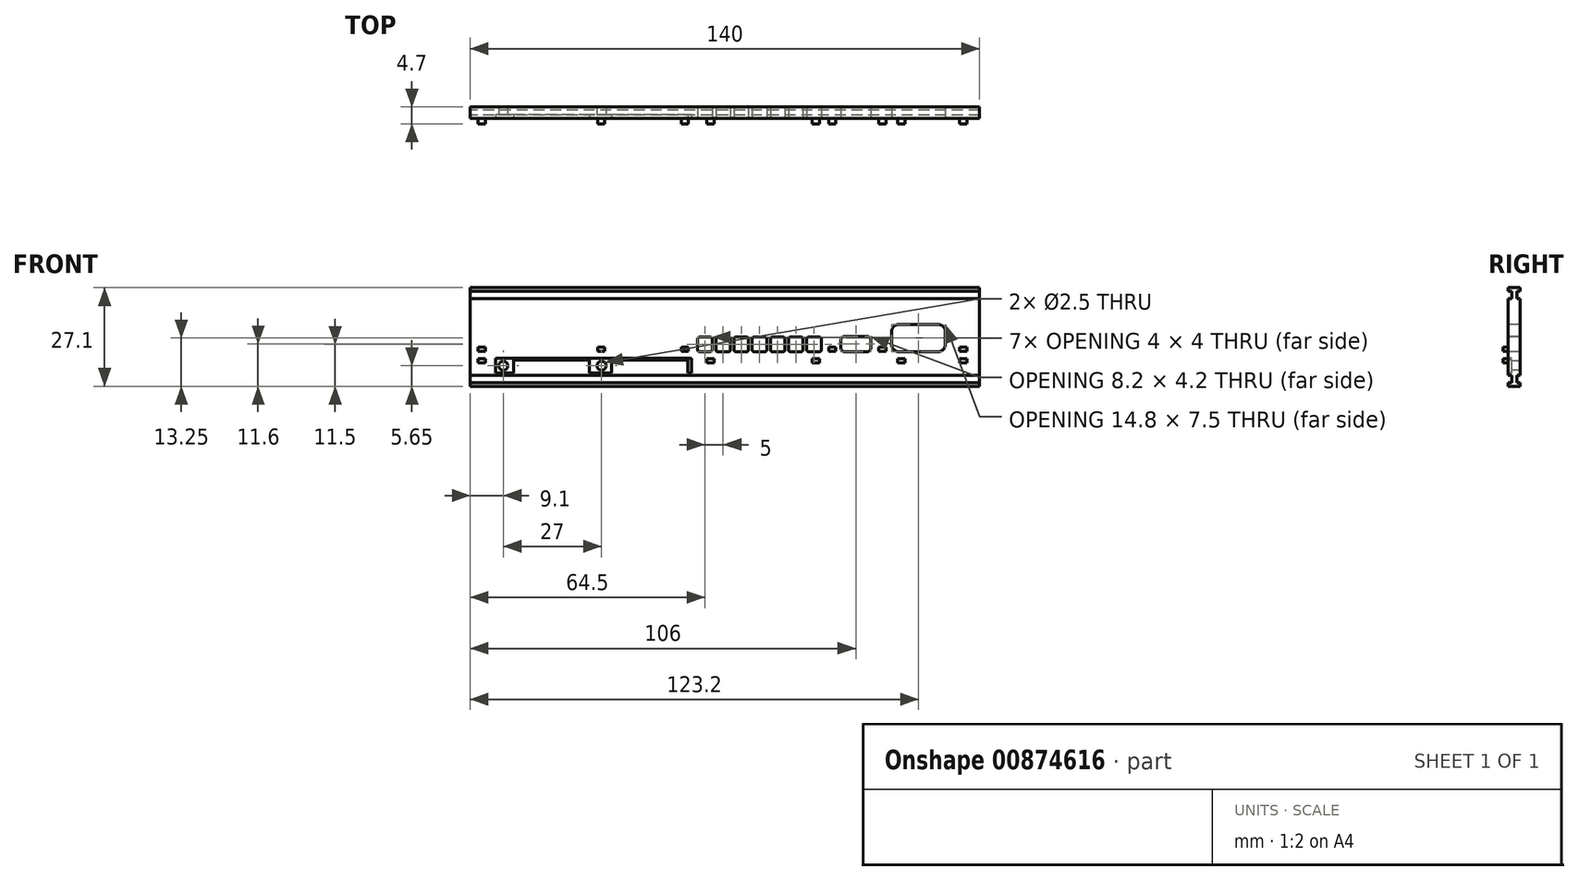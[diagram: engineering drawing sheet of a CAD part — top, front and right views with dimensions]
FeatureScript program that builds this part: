
annotation { "Feature Type Name" : "Feature", "Feature Type Description" : "" }
export const myFeature = defineFeature(function(context is Context, id is Id, definition is map)
    precondition{}
    {
        {
            var Q0;
            Q0=qCreatedBy(makeId("Right.planeOp"),FACE);
            var sketch = newSketch(context, id + "F0", { "sketchPlane" : qUnion([Q0])});
            skLineSegment(sketch, "E0", {"start": v(-1.6, 0) * mm, "end": v(-1.6, 10.55) * mm});
            skLineSegment(sketch, "E1", {"start": v(-1.6, 10.55) * mm, "end": v(-0.7, 10.55) * mm});
            skLineSegment(sketch, "E2", {"start": v(-0.7, 10.55) * mm, "end": v(-0.7, 12.55) * mm});
            skLineSegment(sketch, "E3", {"start": v(-0.7, 12.55) * mm, "end": v(-1.6, 12.55) * mm});
            skLineSegment(sketch, "E4", {"start": v(-1.6, 12.55) * mm, "end": v(-1.6, 13.55) * mm});
            skLineSegment(sketch, "E5", {"start": v(-1.6, 13.55) * mm, "end": v(0, 13.55) * mm});
            skLineSegment(sketch, "E6.MirrorCS", {"start": v(1.6, 13.55) * mm, "end": v(0, 13.55) * mm});
            skLineSegment(sketch, "E7.MirrorCS", {"start": v(1.6, 12.55) * mm, "end": v(1.6, 13.55) * mm});
            skLineSegment(sketch, "E8.MirrorCS", {"start": v(1.6, 10.55) * mm, "end": v(0.7, 10.55) * mm});
            skLineSegment(sketch, "E9.MirrorCS", {"start": v(0.7, 10.55) * mm, "end": v(0.7, 12.55) * mm});
            skLineSegment(sketch, "E10.MirrorCS", {"start": v(1.6, 0) * mm, "end": v(1.6, 10.55) * mm});
            skLineSegment(sketch, "E11.MirrorCS", {"start": v(0.7, 12.55) * mm, "end": v(1.6, 12.55) * mm});
            skLineSegment(sketch, "E12.MirrorCS", {"start": v(1.6, -10.55) * mm, "end": v(0.7, -10.55) * mm});
            skLineSegment(sketch, "E13.MirrorCS", {"start": v(0.7, -10.55) * mm, "end": v(0.7, -12.55) * mm});
            skLineSegment(sketch, "E14.MirrorCS", {"start": v(-0.7, -12.55) * mm, "end": v(-1.6, -12.55) * mm});
            skLineSegment(sketch, "E15.MirrorCS", {"start": v(1.6, -13.55) * mm, "end": v(0, -13.55) * mm});
            skLineSegment(sketch, "E16.MirrorCS", {"start": v(1.6, -12.55) * mm, "end": v(1.6, -13.55) * mm});
            skLineSegment(sketch, "E17.MirrorCS", {"start": v(1.6, 0) * mm, "end": v(1.6, -10.55) * mm});
            skLineSegment(sketch, "E18.MirrorCS", {"start": v(-1.6, -10.55) * mm, "end": v(-0.7, -10.55) * mm});
            skLineSegment(sketch, "E19.MirrorCS", {"start": v(-0.7, -10.55) * mm, "end": v(-0.7, -12.55) * mm});
            skLineSegment(sketch, "E20.MirrorCS", {"start": v(0.7, -12.55) * mm, "end": v(1.6, -12.55) * mm});
            skLineSegment(sketch, "E21.MirrorCS", {"start": v(-1.6, -13.55) * mm, "end": v(0, -13.55) * mm});
            skLineSegment(sketch, "E22.MirrorCS", {"start": v(-1.6, -12.55) * mm, "end": v(-1.6, -13.55) * mm});
            skLineSegment(sketch, "E23.MirrorCS", {"start": v(-1.6, 0) * mm, "end": v(-1.6, -10.55) * mm});
            skSolve(sketch);
        }
        {
            var Q0;
            Q0=makeQuery(id+"F0.imprint","IMPRINT",FACE,{"disambiguationData":[TD([[makeQuery(id+"F0.imprint","IMPRINT",EDGE,{"derivedFrom":sQuery(id+"F0.wireOp",EDGE,"E8.MirrorCS")}),1.0]])]});
            extrude(context, id + "F1", {"entities" : qUnion([Q0]), "endBound" : BoundingType.SYMMETRIC, "depth" : 140 * mm, "offsetDistance" : 25 * mm});
        }
        {
            var Q0;
            Q0=makeQuery(id+"F1.opExtrude","SWEPT_FACE",FACE,{"disambiguationData":[OSD([sQuery(id+"F0.wireOp",EDGE,"E0"),sQuery(id+"F0.wireOp",EDGE,"E23.MirrorCS")])]});
            var sketch = newSketch(context, id + "F2", { "sketchPlane" : qUnion([Q0])});
            skLineSegment(sketch, "E24.bottom", {"start": v(-4, -4.05) * mm, "end": v(-7, -4.05) * mm});
            skLineSegment(sketch, "E24.top", {"start": v(-4, -0.05) * mm, "end": v(-7, -0.05) * mm});
            skLineSegment(sketch, "E24.left", {"start": v(-3.5, -3.55) * mm, "end": v(-3.5, -0.55) * mm});
            skLineSegment(sketch, "E24.right", {"start": v(-7.5, -3.55) * mm, "end": v(-7.5, -0.55) * mm});
            skPoint(sketch, "E24.middle", {"position": v(-5.5, -2.05) * mm});
            skPoint(sketch, "E25.visualSharp", {"position": v(-7.5, -0.05) * mm});
            skArc(sketch, "E25.filletArc", {"start": v(-7, -0.05) * mm, "mid": v(-7.35, -0.2) * mm, "end": v(-7.5, -0.55) * mm});
            skPoint(sketch, "E26.visualSharp", {"position": v(-3.5, -0.05) * mm});
            skArc(sketch, "E26.filletArc", {"start": v(-3.5, -0.55) * mm, "mid": v(-3.65, -0.2) * mm, "end": v(-4, -0.05) * mm});
            skPoint(sketch, "E27.visualSharp", {"position": v(-3.5, -4.05) * mm});
            skArc(sketch, "E27.filletArc", {"start": v(-4, -4.05) * mm, "mid": v(-3.65, -3.9) * mm, "end": v(-3.5, -3.55) * mm});
            skPoint(sketch, "E28.visualSharp", {"position": v(-7.5, -4.05) * mm});
            skArc(sketch, "E28.filletArc", {"start": v(-7.5, -3.55) * mm, "mid": v(-7.35, -3.9) * mm, "end": v(-7, -4.05) * mm});
            skPoint(sketch, "E29.1.0.0", {"position": v(-0.5, -2.05) * mm});
            skLineSegment(sketch, "E29.1.0.1", {"start": v(1, -0.05) * mm, "end": v(-2, -0.05) * mm});
            skLineSegment(sketch, "E29.1.0.2", {"start": v(1, -4.05) * mm, "end": v(-2, -4.05) * mm});
            skPoint(sketch, "E29.1.0.3", {"position": v(-2.5, -0.05) * mm});
            skLineSegment(sketch, "E29.1.0.4", {"start": v(-2.5, -3.55) * mm, "end": v(-2.5, -0.55) * mm});
            skPoint(sketch, "E29.1.0.5", {"position": v(1.5, -4.05) * mm});
            skPoint(sketch, "E29.1.0.6", {"position": v(1.5, -0.05) * mm});
            skPoint(sketch, "E29.1.0.7", {"position": v(-2.5, -4.05) * mm});
            skLineSegment(sketch, "E29.1.0.8", {"start": v(1.5, -3.55) * mm, "end": v(1.5, -0.55) * mm});
            skArc(sketch, "E29.1.0.9", {"start": v(1.5, -0.55) * mm, "mid": v(1.35, -0.2) * mm, "end": v(1, -0.05) * mm});
            skArc(sketch, "E29.1.0.10", {"start": v(1, -4.05) * mm, "mid": v(1.35, -3.9) * mm, "end": v(1.5, -3.55) * mm});
            skArc(sketch, "E29.1.0.11", {"start": v(-2, -0.05) * mm, "mid": v(-2.35, -0.2) * mm, "end": v(-2.5, -0.55) * mm});
            skArc(sketch, "E29.1.0.12", {"start": v(-2.5, -3.55) * mm, "mid": v(-2.35, -3.9) * mm, "end": v(-2, -4.05) * mm});
            skPoint(sketch, "E29.2.0.0", {"position": v(4.5, -2.05) * mm});
            skLineSegment(sketch, "E29.2.0.1", {"start": v(6, -0.05) * mm, "end": v(3, -0.05) * mm});
            skLineSegment(sketch, "E29.2.0.2", {"start": v(6, -4.05) * mm, "end": v(3, -4.05) * mm});
            skPoint(sketch, "E29.2.0.3", {"position": v(2.5, -0.05) * mm});
            skLineSegment(sketch, "E29.2.0.4", {"start": v(2.5, -3.55) * mm, "end": v(2.5, -0.55) * mm});
            skPoint(sketch, "E29.2.0.5", {"position": v(6.5, -4.05) * mm});
            skPoint(sketch, "E29.2.0.6", {"position": v(6.5, -0.05) * mm});
            skPoint(sketch, "E29.2.0.7", {"position": v(2.5, -4.05) * mm});
            skLineSegment(sketch, "E29.2.0.8", {"start": v(6.5, -3.55) * mm, "end": v(6.5, -0.55) * mm});
            skArc(sketch, "E29.2.0.9", {"start": v(6.5, -0.55) * mm, "mid": v(6.35, -0.2) * mm, "end": v(6, -0.05) * mm});
            skArc(sketch, "E29.2.0.10", {"start": v(6, -4.05) * mm, "mid": v(6.35, -3.9) * mm, "end": v(6.5, -3.55) * mm});
            skArc(sketch, "E29.2.0.11", {"start": v(3, -0.05) * mm, "mid": v(2.65, -0.2) * mm, "end": v(2.5, -0.55) * mm});
            skArc(sketch, "E29.2.0.12", {"start": v(2.5, -3.55) * mm, "mid": v(2.65, -3.9) * mm, "end": v(3, -4.05) * mm});
            skPoint(sketch, "E29.3.0.0", {"position": v(9.5, -2.05) * mm});
            skLineSegment(sketch, "E29.3.0.1", {"start": v(11, -0.05) * mm, "end": v(8, -0.05) * mm});
            skLineSegment(sketch, "E29.3.0.2", {"start": v(11, -4.05) * mm, "end": v(8, -4.05) * mm});
            skPoint(sketch, "E29.3.0.3", {"position": v(7.5, -0.05) * mm});
            skLineSegment(sketch, "E29.3.0.4", {"start": v(7.5, -3.55) * mm, "end": v(7.5, -0.55) * mm});
            skPoint(sketch, "E29.3.0.5", {"position": v(11.5, -4.05) * mm});
            skPoint(sketch, "E29.3.0.6", {"position": v(11.5, -0.05) * mm});
            skPoint(sketch, "E29.3.0.7", {"position": v(7.5, -4.05) * mm});
            skLineSegment(sketch, "E29.3.0.8", {"start": v(11.5, -3.55) * mm, "end": v(11.5, -0.55) * mm});
            skArc(sketch, "E29.3.0.9", {"start": v(11.5, -0.55) * mm, "mid": v(11.35, -0.2) * mm, "end": v(11, -0.05) * mm});
            skArc(sketch, "E29.3.0.10", {"start": v(11, -4.05) * mm, "mid": v(11.35, -3.9) * mm, "end": v(11.5, -3.55) * mm});
            skArc(sketch, "E29.3.0.11", {"start": v(8, -0.05) * mm, "mid": v(7.65, -0.2) * mm, "end": v(7.5, -0.55) * mm});
            skArc(sketch, "E29.3.0.12", {"start": v(7.5, -3.55) * mm, "mid": v(7.65, -3.9) * mm, "end": v(8, -4.05) * mm});
            skPoint(sketch, "E29.4.0.0", {"position": v(14.5, -2.05) * mm});
            skLineSegment(sketch, "E29.4.0.1", {"start": v(16, -0.05) * mm, "end": v(13, -0.05) * mm});
            skLineSegment(sketch, "E29.4.0.2", {"start": v(16, -4.05) * mm, "end": v(13, -4.05) * mm});
            skPoint(sketch, "E29.4.0.3", {"position": v(12.5, -0.05) * mm});
            skLineSegment(sketch, "E29.4.0.4", {"start": v(12.5, -3.55) * mm, "end": v(12.5, -0.55) * mm});
            skPoint(sketch, "E29.4.0.5", {"position": v(16.5, -4.05) * mm});
            skPoint(sketch, "E29.4.0.6", {"position": v(16.5, -0.05) * mm});
            skPoint(sketch, "E29.4.0.7", {"position": v(12.5, -4.05) * mm});
            skLineSegment(sketch, "E29.4.0.8", {"start": v(16.5, -3.55) * mm, "end": v(16.5, -0.55) * mm});
            skArc(sketch, "E29.4.0.9", {"start": v(16.5, -0.55) * mm, "mid": v(16.35, -0.2) * mm, "end": v(16, -0.05) * mm});
            skArc(sketch, "E29.4.0.10", {"start": v(16, -4.05) * mm, "mid": v(16.35, -3.9) * mm, "end": v(16.5, -3.55) * mm});
            skArc(sketch, "E29.4.0.11", {"start": v(13, -0.05) * mm, "mid": v(12.65, -0.2) * mm, "end": v(12.5, -0.55) * mm});
            skArc(sketch, "E29.4.0.12", {"start": v(12.5, -3.55) * mm, "mid": v(12.65, -3.9) * mm, "end": v(13, -4.05) * mm});
            skPoint(sketch, "E29.5.0.0", {"position": v(19.5, -2.05) * mm});
            skLineSegment(sketch, "E29.5.0.1", {"start": v(21, -0.05) * mm, "end": v(18, -0.05) * mm});
            skLineSegment(sketch, "E29.5.0.2", {"start": v(21, -4.05) * mm, "end": v(18, -4.05) * mm});
            skPoint(sketch, "E29.5.0.3", {"position": v(17.5, -0.05) * mm});
            skLineSegment(sketch, "E29.5.0.4", {"start": v(17.5, -3.55) * mm, "end": v(17.5, -0.55) * mm});
            skPoint(sketch, "E29.5.0.5", {"position": v(21.5, -4.05) * mm});
            skPoint(sketch, "E29.5.0.6", {"position": v(21.5, -0.05) * mm});
            skPoint(sketch, "E29.5.0.7", {"position": v(17.5, -4.05) * mm});
            skLineSegment(sketch, "E29.5.0.8", {"start": v(21.5, -3.55) * mm, "end": v(21.5, -0.55) * mm});
            skArc(sketch, "E29.5.0.9", {"start": v(21.5, -0.55) * mm, "mid": v(21.35, -0.2) * mm, "end": v(21, -0.05) * mm});
            skArc(sketch, "E29.5.0.10", {"start": v(21, -4.05) * mm, "mid": v(21.35, -3.9) * mm, "end": v(21.5, -3.55) * mm});
            skArc(sketch, "E29.5.0.11", {"start": v(18, -0.05) * mm, "mid": v(17.65, -0.2) * mm, "end": v(17.5, -0.55) * mm});
            skArc(sketch, "E29.5.0.12", {"start": v(17.5, -3.55) * mm, "mid": v(17.65, -3.9) * mm, "end": v(18, -4.05) * mm});
            skPoint(sketch, "E29.6.0.0", {"position": v(24.5, -2.05) * mm});
            skLineSegment(sketch, "E29.6.0.1", {"start": v(26, -0.05) * mm, "end": v(23, -0.05) * mm});
            skLineSegment(sketch, "E29.6.0.2", {"start": v(26, -4.05) * mm, "end": v(23, -4.05) * mm});
            skPoint(sketch, "E29.6.0.3", {"position": v(22.5, -0.05) * mm});
            skLineSegment(sketch, "E29.6.0.4", {"start": v(22.5, -3.55) * mm, "end": v(22.5, -0.55) * mm});
            skPoint(sketch, "E29.6.0.5", {"position": v(26.5, -4.05) * mm});
            skPoint(sketch, "E29.6.0.6", {"position": v(26.5, -0.05) * mm});
            skPoint(sketch, "E29.6.0.7", {"position": v(22.5, -4.05) * mm});
            skLineSegment(sketch, "E29.6.0.8", {"start": v(26.5, -3.55) * mm, "end": v(26.5, -0.55) * mm});
            skArc(sketch, "E29.6.0.9", {"start": v(26.5, -0.55) * mm, "mid": v(26.35, -0.2) * mm, "end": v(26, -0.05) * mm});
            skArc(sketch, "E29.6.0.10", {"start": v(26, -4.05) * mm, "mid": v(26.35, -3.9) * mm, "end": v(26.5, -3.55) * mm});
            skArc(sketch, "E29.6.0.11", {"start": v(23, -0.05) * mm, "mid": v(22.65, -0.2) * mm, "end": v(22.5, -0.55) * mm});
            skArc(sketch, "E29.6.0.12", {"start": v(22.5, -3.55) * mm, "mid": v(22.65, -3.9) * mm, "end": v(23, -4.05) * mm});
            skLineSegment(sketch, "E29.direction1", {"start": v(-7.5, -4.05) * mm, "end": v(-2.5, -4.05) * mm, "construction": true});
            skLineSegment(sketch, "E30.bottom", {"start": v(39.1, -4.05) * mm, "end": v(32.9, -4.05) * mm});
            skLineSegment(sketch, "E30.top", {"start": v(39.1, 0.15) * mm, "end": v(32.9, 0.15) * mm});
            skLineSegment(sketch, "E30.left", {"start": v(40.1, -3.05) * mm, "end": v(40.1, -0.85) * mm});
            skLineSegment(sketch, "E30.right", {"start": v(31.9, -3.05) * mm, "end": v(31.9, -0.85) * mm});
            skPoint(sketch, "E30.middle", {"position": v(36, -1.95) * mm});
            skLineSegment(sketch, "E31.bottom", {"start": v(58.6, -4.05) * mm, "end": v(47.8, -4.05) * mm});
            skLineSegment(sketch, "E31.top", {"start": v(58.6, 3.45) * mm, "end": v(47.8, 3.45) * mm});
            skLineSegment(sketch, "E31.left", {"start": v(60.6, -2.05) * mm, "end": v(60.6, 1.45) * mm});
            skLineSegment(sketch, "E31.right", {"start": v(45.8, -2.05) * mm, "end": v(45.8, 1.45) * mm});
            skPoint(sketch, "E31.middle", {"position": v(53.2, -0.3) * mm});
            skPoint(sketch, "E32.visualSharp", {"position": v(31.9, 0.15) * mm});
            skArc(sketch, "E32.filletArc", {"start": v(32.9, 0.15) * mm, "mid": v(32.2, -0.14) * mm, "end": v(31.9, -0.85) * mm});
            skPoint(sketch, "E33.visualSharp", {"position": v(40.1, 0.15) * mm});
            skArc(sketch, "E33.filletArc", {"start": v(40.1, -0.85) * mm, "mid": v(39.8, -0.14) * mm, "end": v(39.1, 0.15) * mm});
            skPoint(sketch, "E34.visualSharp", {"position": v(40.1, -4.05) * mm});
            skArc(sketch, "E34.filletArc", {"start": v(39.1, -4.05) * mm, "mid": v(39.8, -3.76) * mm, "end": v(40.1, -3.05) * mm});
            skPoint(sketch, "E35.visualSharp", {"position": v(31.9, -4.05) * mm});
            skArc(sketch, "E35.filletArc", {"start": v(31.9, -3.05) * mm, "mid": v(32.2, -3.76) * mm, "end": v(32.9, -4.05) * mm});
            skPoint(sketch, "E36.visualSharp", {"position": v(45.8, 3.45) * mm});
            skArc(sketch, "E36.filletArc", {"start": v(47.8, 3.45) * mm, "mid": v(46.39, 2.86) * mm, "end": v(45.8, 1.45) * mm});
            skPoint(sketch, "E37.visualSharp", {"position": v(60.6, 3.45) * mm});
            skArc(sketch, "E37.filletArc", {"start": v(60.6, 1.45) * mm, "mid": v(60.01, 2.86) * mm, "end": v(58.6, 3.45) * mm});
            skPoint(sketch, "E38.visualSharp", {"position": v(60.6, -4.05) * mm});
            skArc(sketch, "E38.filletArc", {"start": v(58.6, -4.05) * mm, "mid": v(60.01, -3.46) * mm, "end": v(60.6, -2.05) * mm});
            skPoint(sketch, "E39.visualSharp", {"position": v(45.8, -4.05) * mm});
            skArc(sketch, "E39.filletArc", {"start": v(45.8, -2.05) * mm, "mid": v(46.39, -3.46) * mm, "end": v(47.8, -4.05) * mm});
            skLineSegment(sketch, "E40.bottom", {"start": v(-9.2, -9.95) * mm, "end": v(-63, -9.95) * mm});
            skLineSegment(sketch, "E40.top", {"start": v(-9.2, -5.85) * mm, "end": v(-63, -5.85) * mm});
            skLineSegment(sketch, "E40.left", {"start": v(-9.2, -9.95) * mm, "end": v(-9.2, -5.85) * mm});
            skLineSegment(sketch, "E40.right", {"start": v(-63, -9.95) * mm, "end": v(-63, -5.85) * mm});
            skPoint(sketch, "E40.middle", {"position": v(-36.1, -7.9) * mm});
            skLineSegment(sketch, "E41.bottom", {"start": v(-37.2, -9.95) * mm, "end": v(-58.1, -9.95) * mm});
            skLineSegment(sketch, "E41.top", {"start": v(-37.2, -6.35) * mm, "end": v(-58.1, -6.35) * mm});
            skLineSegment(sketch, "E41.left", {"start": v(-37.2, -9.95) * mm, "end": v(-37.2, -6.35) * mm});
            skLineSegment(sketch, "E41.right", {"start": v(-58.1, -9.95) * mm, "end": v(-58.1, -6.35) * mm});
            skPoint(sketch, "E41.middle", {"position": v(-47.65, -8.15) * mm});
            skLineSegment(sketch, "E42.bottom", {"start": v(-10.2, -9.95) * mm, "end": v(-31.1, -9.95) * mm});
            skLineSegment(sketch, "E42.top", {"start": v(-10.2, -6.35) * mm, "end": v(-31.1, -6.35) * mm});
            skLineSegment(sketch, "E42.left", {"start": v(-10.2, -9.95) * mm, "end": v(-10.2, -6.35) * mm});
            skLineSegment(sketch, "E42.right", {"start": v(-31.1, -9.95) * mm, "end": v(-31.1, -6.35) * mm});
            skPoint(sketch, "E42.middle", {"position": v(-20.65, -8.15) * mm});
            skCircle(sketch, "E43", {"center": v(-60.9, -7.9) * mm, "radius": 1.25 * mm});
            skPoint(sketch, "E43.centerSnap0", {"position": v(-63, -7.9) * mm});
            skCircle(sketch, "E44", {"center": v(-33.9, -7.9) * mm, "radius": 1.25 * mm});
            skLineSegment(sketch, "E45.bottom", {"start": v(66.5, -3.95) * mm, "end": v(64.5, -3.95) * mm});
            skLineSegment(sketch, "E45.top", {"start": v(66.5, -2.75) * mm, "end": v(64.5, -2.75) * mm});
            skLineSegment(sketch, "E45.left", {"start": v(66.5, -3.95) * mm, "end": v(66.5, -2.75) * mm});
            skLineSegment(sketch, "E45.right", {"start": v(64.5, -3.95) * mm, "end": v(64.5, -2.75) * mm});
            skPoint(sketch, "E45.middle", {"position": v(65.5, -3.35) * mm});
            skLineSegment(sketch, "E46.bottom", {"start": v(66.5, -7.15) * mm, "end": v(64.5, -7.15) * mm});
            skLineSegment(sketch, "E46.top", {"start": v(66.5, -5.95) * mm, "end": v(64.5, -5.95) * mm});
            skLineSegment(sketch, "E46.left", {"start": v(66.5, -7.15) * mm, "end": v(66.5, -5.95) * mm});
            skLineSegment(sketch, "E46.right", {"start": v(64.5, -7.15) * mm, "end": v(64.5, -5.95) * mm});
            skPoint(sketch, "E46.middle", {"position": v(65.5, -6.55) * mm});
            skLineSegment(sketch, "E47.bottom", {"start": v(44.3, -3.95) * mm, "end": v(42.3, -3.95) * mm});
            skLineSegment(sketch, "E47.top", {"start": v(44.3, -2.75) * mm, "end": v(42.3, -2.75) * mm});
            skLineSegment(sketch, "E47.left", {"start": v(44.3, -3.95) * mm, "end": v(44.3, -2.75) * mm});
            skLineSegment(sketch, "E47.right", {"start": v(42.3, -3.95) * mm, "end": v(42.3, -2.75) * mm});
            skPoint(sketch, "E47.middle", {"position": v(43.3, -3.35) * mm});
            skLineSegment(sketch, "E48.bottom", {"start": v(49.5, -7.15) * mm, "end": v(47.5, -7.15) * mm});
            skLineSegment(sketch, "E48.top", {"start": v(49.5, -5.95) * mm, "end": v(47.5, -5.95) * mm});
            skLineSegment(sketch, "E48.left", {"start": v(49.5, -7.15) * mm, "end": v(49.5, -5.95) * mm});
            skLineSegment(sketch, "E48.right", {"start": v(47.5, -7.15) * mm, "end": v(47.5, -5.95) * mm});
            skPoint(sketch, "E48.middle", {"position": v(48.5, -6.55) * mm});
            skLineSegment(sketch, "E49.bottom", {"start": v(26, -7.15) * mm, "end": v(24, -7.15) * mm});
            skLineSegment(sketch, "E49.top", {"start": v(26, -5.95) * mm, "end": v(24, -5.95) * mm});
            skLineSegment(sketch, "E49.left", {"start": v(26, -7.15) * mm, "end": v(26, -5.95) * mm});
            skLineSegment(sketch, "E49.right", {"start": v(24, -7.15) * mm, "end": v(24, -5.95) * mm});
            skPoint(sketch, "E49.middle", {"position": v(25, -6.55) * mm});
            skLineSegment(sketch, "E50.bottom", {"start": v(30.5, -3.95) * mm, "end": v(28.5, -3.95) * mm});
            skLineSegment(sketch, "E50.top", {"start": v(30.5, -2.75) * mm, "end": v(28.5, -2.75) * mm});
            skLineSegment(sketch, "E50.left", {"start": v(30.5, -3.95) * mm, "end": v(30.5, -2.75) * mm});
            skLineSegment(sketch, "E50.right", {"start": v(28.5, -3.95) * mm, "end": v(28.5, -2.75) * mm});
            skPoint(sketch, "E50.middle", {"position": v(29.5, -3.35) * mm});
            skLineSegment(sketch, "E51.bottom", {"start": v(-65.8, -7.15) * mm, "end": v(-67.8, -7.15) * mm});
            skLineSegment(sketch, "E51.top", {"start": v(-65.8, -5.95) * mm, "end": v(-67.8, -5.95) * mm});
            skLineSegment(sketch, "E51.left", {"start": v(-65.8, -7.15) * mm, "end": v(-65.8, -5.95) * mm});
            skLineSegment(sketch, "E51.right", {"start": v(-67.8, -7.15) * mm, "end": v(-67.8, -5.95) * mm});
            skPoint(sketch, "E51.middle", {"position": v(-66.8, -6.55) * mm});
            skLineSegment(sketch, "E52.bottom", {"start": v(-65.8, -3.95) * mm, "end": v(-67.8, -3.95) * mm});
            skLineSegment(sketch, "E52.top", {"start": v(-65.8, -2.75) * mm, "end": v(-67.8, -2.75) * mm});
            skLineSegment(sketch, "E52.left", {"start": v(-65.8, -3.95) * mm, "end": v(-65.8, -2.75) * mm});
            skLineSegment(sketch, "E52.right", {"start": v(-67.8, -3.95) * mm, "end": v(-67.8, -2.75) * mm});
            skPoint(sketch, "E52.middle", {"position": v(-66.8, -3.35) * mm});
            skLineSegment(sketch, "E53.bottom", {"start": v(-33, -3.95) * mm, "end": v(-35, -3.95) * mm});
            skLineSegment(sketch, "E53.top", {"start": v(-33, -2.75) * mm, "end": v(-35, -2.75) * mm});
            skLineSegment(sketch, "E53.left", {"start": v(-33, -3.95) * mm, "end": v(-33, -2.75) * mm});
            skLineSegment(sketch, "E53.right", {"start": v(-35, -3.95) * mm, "end": v(-35, -2.75) * mm});
            skPoint(sketch, "E53.middle", {"position": v(-34, -3.35) * mm});
            skLineSegment(sketch, "E54.bottom", {"start": v(-10, -3.95) * mm, "end": v(-12, -3.95) * mm});
            skLineSegment(sketch, "E54.top", {"start": v(-10, -2.75) * mm, "end": v(-12, -2.75) * mm});
            skLineSegment(sketch, "E54.left", {"start": v(-10, -3.95) * mm, "end": v(-10, -2.75) * mm});
            skLineSegment(sketch, "E54.right", {"start": v(-12, -3.95) * mm, "end": v(-12, -2.75) * mm});
            skPoint(sketch, "E54.middle", {"position": v(-11, -3.35) * mm});
            skLineSegment(sketch, "E55.bottom", {"start": v(-3, -7.15) * mm, "end": v(-5, -7.15) * mm});
            skLineSegment(sketch, "E55.top", {"start": v(-3, -5.95) * mm, "end": v(-5, -5.95) * mm});
            skLineSegment(sketch, "E55.left", {"start": v(-3, -7.15) * mm, "end": v(-3, -5.95) * mm});
            skLineSegment(sketch, "E55.right", {"start": v(-5, -7.15) * mm, "end": v(-5, -5.95) * mm});
            skPoint(sketch, "E55.middle", {"position": v(-4, -6.55) * mm});
            skSolve(sketch);
        }
        {
            var Q0;
            Q0=makeQuery(id+"F2.imprint","IMPRINT",FACE,{"disambiguationData":[TD([[makeQuery(id+"F2.imprint","IMPRINT",EDGE,{"derivedFrom":sQuery(id+"F2.wireOp",EDGE,"E24.bottom")}),-1.0]])]});
            var Q1;
            Q1=makeQuery(id+"F2.imprint","IMPRINT",FACE,{"disambiguationData":[TD([[makeQuery(id+"F2.imprint","IMPRINT",EDGE,{"derivedFrom":sQuery(id+"F2.wireOp",EDGE,"E29.1.0.1")}),1.0]])]});
            var Q2;
            Q2=makeQuery(id+"F2.imprint","IMPRINT",FACE,{"disambiguationData":[TD([[makeQuery(id+"F2.imprint","IMPRINT",EDGE,{"derivedFrom":sQuery(id+"F2.wireOp",EDGE,"E29.2.0.1")}),1.0]])]});
            var Q3;
            Q3=makeQuery(id+"F2.imprint","IMPRINT",FACE,{"disambiguationData":[TD([[makeQuery(id+"F2.imprint","IMPRINT",EDGE,{"derivedFrom":sQuery(id+"F2.wireOp",EDGE,"E29.3.0.1")}),1.0]])]});
            var Q4;
            Q4=makeQuery(id+"F2.imprint","IMPRINT",FACE,{"disambiguationData":[TD([[makeQuery(id+"F2.imprint","IMPRINT",EDGE,{"derivedFrom":sQuery(id+"F2.wireOp",EDGE,"E29.4.0.1")}),1.0]])]});
            var Q5;
            Q5=makeQuery(id+"F2.imprint","IMPRINT",FACE,{"disambiguationData":[TD([[makeQuery(id+"F2.imprint","IMPRINT",EDGE,{"derivedFrom":sQuery(id+"F2.wireOp",EDGE,"E29.5.0.1")}),1.0]])]});
            var Q6;
            Q6=makeQuery(id+"F2.imprint","IMPRINT",FACE,{"disambiguationData":[TD([[makeQuery(id+"F2.imprint","IMPRINT",EDGE,{"derivedFrom":sQuery(id+"F2.wireOp",EDGE,"E29.6.0.1")}),1.0]])]});
            var Q7;
            Q7=makeQuery(id+"F2.imprint","IMPRINT",FACE,{"disambiguationData":[TD([[makeQuery(id+"F2.imprint","IMPRINT",EDGE,{"derivedFrom":sQuery(id+"F2.wireOp",EDGE,"E30.bottom")}),-1.0]])]});
            var Q8;
            Q8=makeQuery(id+"F2.imprint","IMPRINT",FACE,{"disambiguationData":[TD([[makeQuery(id+"F2.imprint","IMPRINT",EDGE,{"derivedFrom":sQuery(id+"F2.wireOp",EDGE,"E31.bottom")}),-1.0]])]});
            var Q9;
            Q9=makeQuery(id+"F2.imprint","IMPRINT",FACE,{"disambiguationData":[TD([[makeQuery(id+"F2.imprint","IMPRINT",EDGE,{"derivedFrom":sQuery(id+"F2.wireOp",EDGE,"E44")}),1.0]])]});
            var Q10;
            Q10=makeQuery(id+"F2.imprint","IMPRINT",FACE,{"disambiguationData":[TD([[makeQuery(id+"F2.imprint","IMPRINT",EDGE,{"derivedFrom":sQuery(id+"F2.wireOp",EDGE,"E42.bottom")}),-1.0]])]});
            var Q11;
            Q11=makeQuery(id+"F2.imprint","IMPRINT",FACE,{"disambiguationData":[TD([[makeQuery(id+"F2.imprint","IMPRINT",EDGE,{"derivedFrom":sQuery(id+"F2.wireOp",EDGE,"E41.bottom")}),-1.0]])]});
            var Q12;
            Q12=makeQuery(id+"F2.imprint","IMPRINT",FACE,{"disambiguationData":[TD([[makeQuery(id+"F2.imprint","IMPRINT",EDGE,{"derivedFrom":sQuery(id+"F2.wireOp",EDGE,"E43")}),1.0]])]});
            extrude(context, id + "F3", {"entities" : qUnion([Q0, Q1, Q2, Q3, Q4, Q5, Q6, Q7, Q8, Q9, Q10, Q11, Q12]), "operationType" : NewBodyOperationType.REMOVE, "oppositeDirection" : true, "depth" : 4 * mm, "offsetDistance" : 25 * mm});
        }
        {
            var Q0;
            Q0=makeQuery(id+"F2.imprint","IMPRINT",FACE,{"disambiguationData":[TD([[makeQuery(id+"F2.imprint","IMPRINT",EDGE,{"derivedFrom":sQuery(id+"F2.wireOp",EDGE,"E40.top")}),1.0]])]});
            extrude(context, id + "F4", {"entities" : qUnion([Q0]), "operationType" : NewBodyOperationType.REMOVE, "oppositeDirection" : true, "depth" : 1 * mm, "offsetDistance" : 25 * mm});
        }
        {
            var Q0;
            Q0=makeQuery(id+"F2.imprint","IMPRINT",FACE,{"disambiguationData":[TD([[makeQuery(id+"F2.imprint","IMPRINT",EDGE,{"derivedFrom":sQuery(id+"F2.wireOp",EDGE,"E52.bottom")}),-1.0]])]});
            var Q1;
            Q1=makeQuery(id+"F2.imprint","IMPRINT",FACE,{"disambiguationData":[TD([[makeQuery(id+"F2.imprint","IMPRINT",EDGE,{"derivedFrom":sQuery(id+"F2.wireOp",EDGE,"E51.bottom")}),-1.0]])]});
            var Q2;
            Q2=makeQuery(id+"F2.imprint","IMPRINT",FACE,{"disambiguationData":[TD([[makeQuery(id+"F2.imprint","IMPRINT",EDGE,{"derivedFrom":sQuery(id+"F2.wireOp",EDGE,"E53.bottom")}),-1.0]])]});
            var Q3;
            Q3=makeQuery(id+"F2.imprint","IMPRINT",FACE,{"disambiguationData":[TD([[makeQuery(id+"F2.imprint","IMPRINT",EDGE,{"derivedFrom":sQuery(id+"F2.wireOp",EDGE,"E54.bottom")}),-1.0]])]});
            var Q4;
            Q4=makeQuery(id+"F2.imprint","IMPRINT",FACE,{"disambiguationData":[TD([[makeQuery(id+"F2.imprint","IMPRINT",EDGE,{"derivedFrom":sQuery(id+"F2.wireOp",EDGE,"E55.bottom")}),-1.0]])]});
            var Q5;
            Q5=makeQuery(id+"F2.imprint","IMPRINT",FACE,{"disambiguationData":[TD([[makeQuery(id+"F2.imprint","IMPRINT",EDGE,{"derivedFrom":sQuery(id+"F2.wireOp",EDGE,"E49.bottom")}),-1.0]])]});
            var Q6;
            Q6=makeQuery(id+"F2.imprint","IMPRINT",FACE,{"disambiguationData":[TD([[makeQuery(id+"F2.imprint","IMPRINT",EDGE,{"derivedFrom":sQuery(id+"F2.wireOp",EDGE,"E50.bottom")}),-1.0]])]});
            var Q7;
            Q7=makeQuery(id+"F2.imprint","IMPRINT",FACE,{"disambiguationData":[TD([[makeQuery(id+"F2.imprint","IMPRINT",EDGE,{"derivedFrom":sQuery(id+"F2.wireOp",EDGE,"E47.bottom")}),-1.0]])]});
            var Q8;
            Q8=makeQuery(id+"F2.imprint","IMPRINT",FACE,{"disambiguationData":[TD([[makeQuery(id+"F2.imprint","IMPRINT",EDGE,{"derivedFrom":sQuery(id+"F2.wireOp",EDGE,"E48.bottom")}),-1.0]])]});
            var Q9;
            Q9=makeQuery(id+"F2.imprint","IMPRINT",FACE,{"disambiguationData":[TD([[makeQuery(id+"F2.imprint","IMPRINT",EDGE,{"derivedFrom":sQuery(id+"F2.wireOp",EDGE,"E45.bottom")}),-1.0]])]});
            var Q10;
            Q10=makeQuery(id+"F2.imprint","IMPRINT",FACE,{"disambiguationData":[TD([[makeQuery(id+"F2.imprint","IMPRINT",EDGE,{"derivedFrom":sQuery(id+"F2.wireOp",EDGE,"E46.bottom")}),-1.0]])]});
            extrude(context, id + "F5", {"entities" : qUnion([Q0, Q1, Q2, Q3, Q4, Q5, Q6, Q7, Q8, Q9, Q10]), "operationType" : NewBodyOperationType.ADD, "depth" : 1.5 * mm, "offsetDistance" : 25 * mm});
        }
    });
